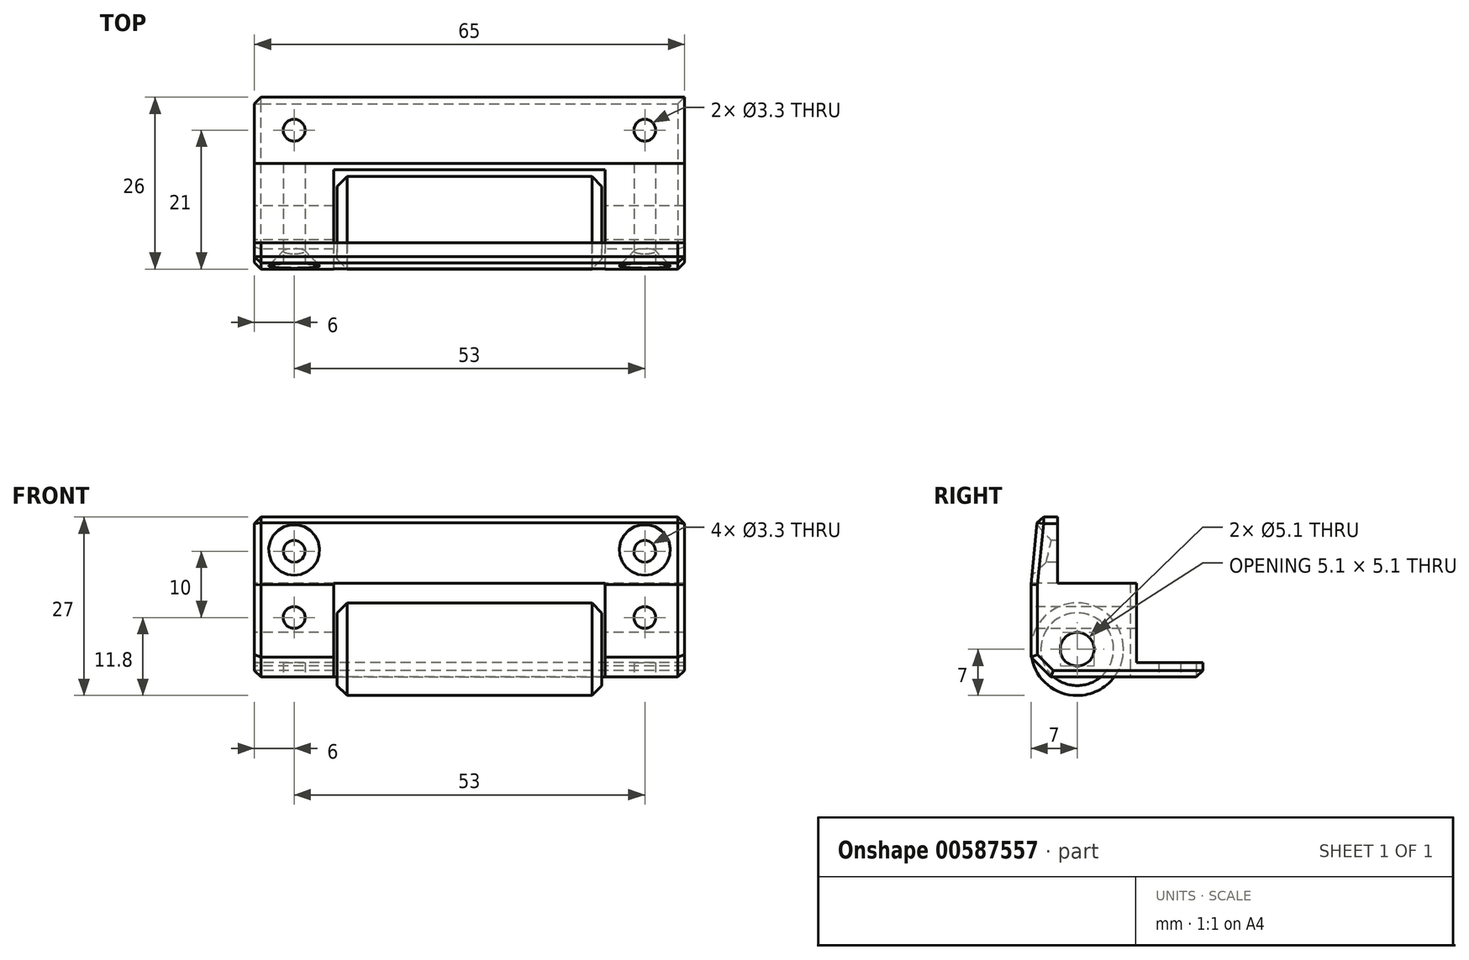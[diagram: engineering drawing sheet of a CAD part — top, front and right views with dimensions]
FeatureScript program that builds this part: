
annotation { "Feature Type Name" : "Feature", "Feature Type Description" : "" }
export const myFeature = defineFeature(function(context is Context, id is Id, definition is map)
    precondition{}
    {
        {
            var Q0;
            Q0=qCreatedBy(makeId("Right.planeOp"),FACE);
            var sketch = newSketch(context, id + "F0", { "sketchPlane" : qUnion([Q0])});
            skLineSegment(sketch, "E0", {"start": v(0, 0) * mm, "end": v(0, 12) * mm});
            skLineSegment(sketch, "E1", {"start": v(0, 12) * mm, "end": v(-12, 12) * mm});
            skLineSegment(sketch, "E2", {"start": v(-12, 12) * mm, "end": v(-12, 22) * mm});
            skLineSegment(sketch, "E3", {"start": v(-12, 22) * mm, "end": v(-15, 22) * mm});
            skLineSegment(sketch, "E4", {"start": v(-16, -2.2) * mm, "end": v(10, -2.2) * mm});
            skLineSegment(sketch, "E5", {"start": v(10, -2.2) * mm, "end": v(10, 0) * mm});
            skLineSegment(sketch, "E6", {"start": v(10, 0) * mm, "end": v(0, 0) * mm});
            skCircle(sketch, "E7", {"center": v(-9, 2) * mm, "radius": 2.55 * mm});
            skCircle(sketch, "E8", {"center": v(-9, 2) * mm, "radius": 7 * mm, "construction": true});
            skLineSegment(sketch, "E9", {"start": v(-16, -2.2) * mm, "end": v(-16, 11.8) * mm});
            skLineSegment(sketch, "E10", {"start": v(-16, 11.8) * mm, "end": v(-15, 22) * mm});
            skSolve(sketch);
        }
        {
            var Q0;
            Q0=makeQuery(id+"F0.imprint","IMPRINT",FACE,{"disambiguationData":[TD([[makeQuery(id+"F0.imprint","IMPRINT",EDGE,{"derivedFrom":sQuery(id+"F0.wireOp",EDGE,"E0")}),1.0]])]});
            extrude(context, id + "F1", {"entities" : qUnion([Q0]), "depth" : 65 * mm, "offsetDistance" : 25 * mm});
        }
        {
            var Q0;
            Q0=makeQuery(id+"F1.opExtrude","SWEPT_FACE",FACE,{"disambiguationData":[OSD([sQuery(id+"F0.wireOp",EDGE,"E9")])]});
            var sketch = newSketch(context, id + "F2", { "sketchPlane" : qUnion([Q0])});
            skLineSegment(sketch, "E11.0.0", {"start": v(0, 22) * mm, "end": v(0, 11.8) * mm, "construction": true});
            skLineSegment(sketch, "E11.0.1", {"start": v(0, 11.8) * mm, "end": v(65, 11.8) * mm, "construction": true});
            skLineSegment(sketch, "E11.0.2", {"start": v(65, 11.8) * mm, "end": v(65, 22) * mm, "construction": true});
            skLineSegment(sketch, "E11.0.3", {"start": v(65, 22) * mm, "end": v(0, 22) * mm, "construction": true});
            skLineSegment(sketch, "E12.0.0", {"start": v(0, 11.8) * mm, "end": v(0, -2.2) * mm, "construction": true});
            skLineSegment(sketch, "E12.0.1", {"start": v(0, -2.2) * mm, "end": v(65, -2.2) * mm, "construction": true});
            skLineSegment(sketch, "E12.0.2", {"start": v(65, -2.2) * mm, "end": v(65, 11.8) * mm, "construction": true});
            skLineSegment(sketch, "E12.0.3", {"start": v(65, 11.8) * mm, "end": v(0, 11.8) * mm, "construction": true});
            skLineSegment(sketch, "E13", {"start": v(32.5, 22) * mm, "end": v(32.5, -2.2) * mm, "construction": true});
            skLineSegment(sketch, "E14.bottom", {"start": v(12, 12) * mm, "end": v(53, 12) * mm});
            skLineSegment(sketch, "E14.top", {"start": v(12, -2.2) * mm, "end": v(53, -2.2) * mm});
            skLineSegment(sketch, "E14.left", {"start": v(12, 12) * mm, "end": v(12, -2.2) * mm});
            skLineSegment(sketch, "E14.right", {"start": v(53, 12) * mm, "end": v(53, -2.2) * mm});
            skLineSegment(sketch, "E15", {"start": v(12, 12) * mm, "end": v(53, -2.2) * mm, "construction": true});
            skLineSegment(sketch, "E16", {"start": v(12, -2.2) * mm, "end": v(53, 12) * mm, "construction": true});
            skPoint(sketch, "E17", {"position": v(32.5, 4.9) * mm});
            skSolve(sketch);
        }
        {
            var Q0;
            Q0=makeQuery(id+"F1.opExtrude","SWEPT_EDGE",EDGE,{"disambiguationData":[OSD([sQuery(id+"F0.wireOp",EDGE,"E4"),sQuery(id+"F0.wireOp",EDGE,"E9")])]});
            chamfer(context, id + "F3", {"entities" : qUnion([Q0]), "width" : 3 * mm, "tangentPropagation" : true});
        }
        {
            var Q0;
            {var subQ0=sQuery(id+"F2.wireOp",EDGE,"E14.top");Q0=makeQuery(id+"F2.imprint","IMPRINT",FACE,{"disambiguationData":[TD([[makeQuery(id+"F2.imprint","IMPRINT",EDGE,{"derivedFrom":subQ0}),-1.0]])]});}
            var Q1;
            {var subQ0=sQuery(id+"F2.wireOp",EDGE,"E14.bottom");Q1=makeQuery(id+"F2.imprint","IMPRINT",FACE,{"disambiguationData":[TD([[makeQuery(id+"F2.imprint","IMPRINT",EDGE,{"derivedFrom":subQ0}),-1.0]])]});}
            extrude(context, id + "F4", {"entities" : qUnion([Q0, Q1]), "operationType" : NewBodyOperationType.REMOVE, "oppositeDirection" : true, "depth" : 15 * mm, "offsetDistance" : 25 * mm});
        }
        {
            var Q0;
            Q0=makeQuery(id+"F4.boolean.opBoolean","COPY",FACE,{"derivedFrom":makeQuery(id+"F4.opExtrude","SWEPT_FACE",FACE,{"disambiguationData":[OSD([sQuery(id+"F2.wireOp",EDGE,"E14.left")])]})});
            cPlane(context, id + "F5", {"entities" : qUnion([Q0]), "cplaneType" : CPlaneType.OFFSET, "offset" : .5 * mm, "width" : 150 * mm, "height" : 150 * mm});
        }
        {
            var Q0;
            Q0=qCreatedBy(id+"F5.planeOp",FACE);
            var sketch = newSketch(context, id + "F6", { "sketchPlane" : qUnion([Q0])});
            skCircle(sketch, "E18.0", {"center": v(-9, 2) * mm, "radius": 2.55 * mm, "construction": true});
            skCircle(sketch, "E19", {"center": v(-9, 2) * mm, "radius": 7 * mm});
            skSolve(sketch);
        }
        {
            var Q0;
            {var subQ1=sQuery(id+"F0.wireOp",EDGE,"E9");Q0=makeQuery(id+"F4.boolean.opBoolean","SPLIT",FACE,{"disambiguationData":[TD([makeQuery(id+"F4.opExtrude","SWEPT_FACE",FACE,{"disambiguationData":[OSD([sQuery(id+"F2.wireOp",EDGE,"E14.left")])]})])],"derivedFrom":makeQuery(id+"F1.opExtrude","SWEPT_FACE",FACE,{"disambiguationData":[OSD([subQ1])]})});}
            var sketch = newSketch(context, id + "F7", { "sketchPlane" : qUnion([Q0])});
            skLineSegment(sketch, "E20.0.0", {"start": v(12, 0.8) * mm, "end": v(12, 11.8) * mm, "construction": true});
            skLineSegment(sketch, "E20.0.1", {"start": v(12, 11.8) * mm, "end": v(0, 11.8) * mm, "construction": true});
            skLineSegment(sketch, "E20.0.2", {"start": v(0, 11.8) * mm, "end": v(0, 0.8) * mm, "construction": true});
            skLineSegment(sketch, "E20.0.3", {"start": v(0, 0.8) * mm, "end": v(12, 0.8) * mm, "construction": true});
            skLineSegment(sketch, "E21.0.0", {"start": v(65, 11.8) * mm, "end": v(53, 11.8) * mm, "construction": true});
            skLineSegment(sketch, "E21.0.1", {"start": v(53, 11.8) * mm, "end": v(53, 0.8) * mm, "construction": true});
            skLineSegment(sketch, "E21.0.2", {"start": v(53, 0.8) * mm, "end": v(65, 0.8) * mm, "construction": true});
            skLineSegment(sketch, "E21.0.3", {"start": v(65, 0.8) * mm, "end": v(65, 11.8) * mm, "construction": true});
            skLineSegment(sketch, "E22", {"start": v(0, 6.8) * mm, "end": v(12, 6.8) * mm, "construction": true});
            skLineSegment(sketch, "E23", {"start": v(53, 6.8) * mm, "end": v(65, 6.8) * mm, "construction": true});
            skCircle(sketch, "E24", {"center": v(59, 6.8) * mm, "radius": 1.65 * mm});
            skCircle(sketch, "E25", {"center": v(6, 6.8) * mm, "radius": 1.65 * mm});
            skLineSegment(sketch, "E26", {"start": v(12, 6.8) * mm, "end": v(53, 6.8) * mm, "construction": true});
            skLineSegment(sketch, "E27", {"start": v(6, 6.8) * mm, "end": v(6, 16.8) * mm, "construction": true});
            skLineSegment(sketch, "E28", {"start": v(59, 6.8) * mm, "end": v(59, 16.8) * mm, "construction": true});
            skPoint(sketch, "E28.endSnap0", {"position": v(59, 11.8) * mm});
            skCircle(sketch, "E29", {"center": v(6, 16.8) * mm, "radius": 1.65 * mm});
            skCircle(sketch, "E30", {"center": v(59, 16.8) * mm, "radius": 1.65 * mm});
            skLineSegment(sketch, "E31", {"start": v(6, 16.8) * mm, "end": v(59, 16.8) * mm, "construction": true});
            skSolve(sketch);
        }
        {
            var Q0;
            Q0=makeQuery(id+"F7.imprint","IMPRINT",FACE,{"disambiguationData":[TD([[makeQuery(id+"F7.imprint","IMPRINT",EDGE,{"derivedFrom":sQuery(id+"F7.wireOp",EDGE,"E25")}),1.0]])]});
            var Q1;
            Q1=makeQuery(id+"F7.imprint","IMPRINT",FACE,{"disambiguationData":[TD([[makeQuery(id+"F7.imprint","IMPRINT",EDGE,{"derivedFrom":sQuery(id+"F7.wireOp",EDGE,"E24")}),1.0]])]});
            var Q2;
            Q2=makeQuery(id+"F7.imprint","IMPRINT",FACE,{"disambiguationData":[TD([[makeQuery(id+"F7.imprint","IMPRINT",EDGE,{"derivedFrom":sQuery(id+"F7.wireOp",EDGE,"E29")}),1.0]])]});
            var Q3;
            Q3=makeQuery(id+"F7.imprint","IMPRINT",FACE,{"disambiguationData":[TD([[makeQuery(id+"F7.imprint","IMPRINT",EDGE,{"derivedFrom":sQuery(id+"F7.wireOp",EDGE,"E30")}),1.0]])]});
            extrude(context, id + "F8", {"entities" : qUnion([Q0, Q1, Q2, Q3]), "operationType" : NewBodyOperationType.REMOVE, "oppositeDirection" : true, "depth" : 25 * mm, "offsetDistance" : 25 * mm});
        }
        {
            var Q0;
            Q0=makeQuery(id+"F6.imprint","IMPRINT",FACE,{"disambiguationData":[TD([[makeQuery(id+"F6.imprint","IMPRINT",EDGE,{"derivedFrom":sQuery(id+"F6.wireOp",EDGE,"E19")}),1.0]])]});
            extrude(context, id + "F9", {"entities" : qUnion([Q0]), "depth" : 40 * mm, "offsetDistance" : 25 * mm});
        }
        {
            var Q0;
            Q0=makeQuery(id+"F9.opExtrude","CAP_EDGE",EDGE,{"disambiguationData":[OSD([sQuery(id+"F6.wireOp",EDGE,"E19")])],"isStart":true});
            var Q1;
            Q1=makeQuery(id+"F9.opExtrude","CAP_EDGE",EDGE,{"disambiguationData":[OSD([sQuery(id+"F6.wireOp",EDGE,"E19")])],"isStart":false});
            chamfer(context, id + "F10", {"entities" : qUnion([Q0, Q1]), "width" : 1.5 * mm, "tangentPropagation" : true});
        }
        {
            var Q0;
            Q0=makeQuery(id+"F1.opExtrude","SWEPT_FACE",FACE,{"disambiguationData":[OSD([sQuery(id+"F0.wireOp",EDGE,"E4")])]});
            var sketch = newSketch(context, id + "F11", { "sketchPlane" : qUnion([Q0])});
            skLineSegment(sketch, "E32.0", {"start": v(65, -10) * mm, "end": v(0, -10) * mm, "construction": true});
            skCircle(sketch, "E33", {"center": v(6, -5) * mm, "radius": 1.65 * mm});
            skCircle(sketch, "E34", {"center": v(59, -5) * mm, "radius": 1.65 * mm});
            skLineSegment(sketch, "E35", {"start": v(6, -5) * mm, "end": v(59, -5) * mm, "construction": true});
            skLineSegment(sketch, "E36", {"start": v(32.5, -5) * mm, "end": v(32.5, -10) * mm, "construction": true});
            skSolve(sketch);
        }
        {
            var Q0;
            Q0=makeQuery(id+"F11.imprint","IMPRINT",FACE,{"disambiguationData":[TD([[makeQuery(id+"F11.imprint","IMPRINT",EDGE,{"derivedFrom":sQuery(id+"F11.wireOp",EDGE,"E33")}),1.0]])]});
            var Q1;
            Q1=makeQuery(id+"F11.imprint","IMPRINT",FACE,{"disambiguationData":[TD([[makeQuery(id+"F11.imprint","IMPRINT",EDGE,{"derivedFrom":sQuery(id+"F11.wireOp",EDGE,"E34")}),1.0]])]});
            extrude(context, id + "F12", {"entities" : qUnion([Q0, Q1]), "operationType" : NewBodyOperationType.REMOVE, "oppositeDirection" : true, "depth" : 25 * mm, "offsetDistance" : 25 * mm});
        }
        {
            var Q0;
            Q0=makeQuery(id+"F8.boolean.opBoolean","COPY",EDGE,{"derivedFrom":makeQuery(id+"F8.opExtrude","CAP_EDGE",EDGE,{"disambiguationData":[OSD([sQuery(id+"F7.wireOp",EDGE,"E25")])],"isStart":true})});
            var Q1;
            Q1=makeQuery(id+"F8.boolean.opBoolean","COPY",EDGE,{"derivedFrom":makeQuery(id+"F8.opExtrude","CAP_EDGE",EDGE,{"disambiguationData":[OSD([sQuery(id+"F7.wireOp",EDGE,"E24")])],"isStart":true})});
            var Q2;
            Q2=makeQuery(id+"F8.boolean.opBoolean","INTERSECT",EDGE,{"derivedFrom":[makeQuery(id+"F1.opExtrude","SWEPT_FACE",FACE,{"disambiguationData":[OSD([sQuery(id+"F0.wireOp",EDGE,"E10")])]}),makeQuery(id+"F8.opExtrude","SWEPT_FACE",FACE,{"disambiguationData":[OSD([sQuery(id+"F7.wireOp",EDGE,"E29")])]})]});
            var Q3;
            Q3=makeQuery(id+"F8.boolean.opBoolean","INTERSECT",EDGE,{"derivedFrom":[makeQuery(id+"F1.opExtrude","SWEPT_FACE",FACE,{"disambiguationData":[OSD([sQuery(id+"F0.wireOp",EDGE,"E10")])]}),makeQuery(id+"F8.opExtrude","SWEPT_FACE",FACE,{"disambiguationData":[OSD([sQuery(id+"F7.wireOp",EDGE,"E30")])]})]});
            var Q4;
            Q4=makeQuery(id+"F12.boolean.opBoolean","COPY",EDGE,{"derivedFrom":makeQuery(id+"F12.opExtrude","CAP_EDGE",EDGE,{"disambiguationData":[OSD([sQuery(id+"F11.wireOp",EDGE,"E33")])],"isStart":true})});
            var Q5;
            Q5=makeQuery(id+"F12.boolean.opBoolean","COPY",EDGE,{"derivedFrom":makeQuery(id+"F12.opExtrude","CAP_EDGE",EDGE,{"disambiguationData":[OSD([sQuery(id+"F11.wireOp",EDGE,"E34")])],"isStart":true})});
            chamfer(context, id + "F13", {"entities" : qUnion([Q0, Q1, Q2, Q3, Q4, Q5]), "width" : 2.2 * mm, "tangentPropagation" : true});
        }
        {
            var Q0;
            Q0=makeQuery(id+"F1.opExtrude","CAP_EDGE",EDGE,{"disambiguationData":[OSD([sQuery(id+"F0.wireOp",EDGE,"E4")])],"isStart":false});
            var Q1;
            Q1=makeQuery(id+"F1.opExtrude","SWEPT_EDGE",EDGE,{"disambiguationData":[OSD([sQuery(id+"F0.wireOp",EDGE,"E4"),sQuery(id+"F0.wireOp",EDGE,"E5")])]});
            var Q2;
            {var subQ0=sQuery(id+"F0.wireOp",EDGE,"E9");var subQ1=sQuery(id+"F0.wireOp",EDGE,"E4");Q2=makeQuery(id+"F3.opChamfer","BLEND_EDGE",EDGE,{"blendedFrom":[makeQuery(id+"F1.opExtrude","SWEPT_EDGE",EDGE,{"disambiguationData":[OSD([subQ1,subQ0])]}),makeQuery(id+"F1.opExtrude","CAP_FACE",FACE,{"disambiguationData":[OSD([sQuery(id+"F0.wireOp",EDGE,"E0"),sQuery(id+"F0.wireOp",EDGE,"E1"),sQuery(id+"F0.wireOp",EDGE,"E2"),sQuery(id+"F0.wireOp",EDGE,"E3"),subQ1,sQuery(id+"F0.wireOp",EDGE,"E5"),sQuery(id+"F0.wireOp",EDGE,"E6"),sQuery(id+"F0.wireOp",EDGE,"E7"),subQ0,sQuery(id+"F0.wireOp",EDGE,"E10")])],"isStart":false})],"blendedInto":[makeQuery(id+"F1.opExtrude","CAP_FACE",FACE,{"disambiguationData":[OSD([sQuery(id+"F0.wireOp",EDGE,"E0"),sQuery(id+"F0.wireOp",EDGE,"E1"),sQuery(id+"F0.wireOp",EDGE,"E2"),sQuery(id+"F0.wireOp",EDGE,"E3"),subQ1,sQuery(id+"F0.wireOp",EDGE,"E5"),sQuery(id+"F0.wireOp",EDGE,"E6"),sQuery(id+"F0.wireOp",EDGE,"E7"),subQ0,sQuery(id+"F0.wireOp",EDGE,"E10")])],"isStart":false})]});}
            var Q3;
            Q3=makeQuery(id+"F1.opExtrude","CAP_EDGE",EDGE,{"disambiguationData":[OSD([sQuery(id+"F0.wireOp",EDGE,"E9")])],"isStart":false});
            var Q4;
            Q4=makeQuery(id+"F1.opExtrude","CAP_EDGE",EDGE,{"disambiguationData":[OSD([sQuery(id+"F0.wireOp",EDGE,"E10")])],"isStart":false});
            var Q5;
            Q5=makeQuery(id+"F1.opExtrude","CAP_EDGE",EDGE,{"disambiguationData":[OSD([sQuery(id+"F0.wireOp",EDGE,"E3")])],"isStart":false});
            var Q6;
            Q6=makeQuery(id+"F1.opExtrude","CAP_EDGE",EDGE,{"disambiguationData":[OSD([sQuery(id+"F0.wireOp",EDGE,"E4")])],"isStart":true});
            var Q7;
            Q7=makeQuery(id+"F1.opExtrude","CAP_EDGE",EDGE,{"disambiguationData":[OSD([sQuery(id+"F0.wireOp",EDGE,"E5")])],"isStart":true});
            var Q8;
            {var subQ0=sQuery(id+"F0.wireOp",EDGE,"E9");var subQ1=sQuery(id+"F0.wireOp",EDGE,"E4");Q8=makeQuery(id+"F3.opChamfer","BLEND_EDGE",EDGE,{"blendedFrom":[makeQuery(id+"F1.opExtrude","SWEPT_EDGE",EDGE,{"disambiguationData":[OSD([subQ1,subQ0])]}),makeQuery(id+"F1.opExtrude","CAP_FACE",FACE,{"disambiguationData":[OSD([sQuery(id+"F0.wireOp",EDGE,"E0"),sQuery(id+"F0.wireOp",EDGE,"E1"),sQuery(id+"F0.wireOp",EDGE,"E2"),sQuery(id+"F0.wireOp",EDGE,"E3"),subQ1,sQuery(id+"F0.wireOp",EDGE,"E5"),sQuery(id+"F0.wireOp",EDGE,"E6"),sQuery(id+"F0.wireOp",EDGE,"E7"),subQ0,sQuery(id+"F0.wireOp",EDGE,"E10")])],"isStart":true})],"blendedInto":[makeQuery(id+"F1.opExtrude","CAP_FACE",FACE,{"disambiguationData":[OSD([sQuery(id+"F0.wireOp",EDGE,"E0"),sQuery(id+"F0.wireOp",EDGE,"E1"),sQuery(id+"F0.wireOp",EDGE,"E2"),sQuery(id+"F0.wireOp",EDGE,"E3"),subQ1,sQuery(id+"F0.wireOp",EDGE,"E5"),sQuery(id+"F0.wireOp",EDGE,"E6"),sQuery(id+"F0.wireOp",EDGE,"E7"),subQ0,sQuery(id+"F0.wireOp",EDGE,"E10")])],"isStart":true})]});}
            var Q9;
            Q9=makeQuery(id+"F1.opExtrude","CAP_EDGE",EDGE,{"disambiguationData":[OSD([sQuery(id+"F0.wireOp",EDGE,"E9")])],"isStart":true});
            var Q10;
            Q10=makeQuery(id+"F1.opExtrude","CAP_EDGE",EDGE,{"disambiguationData":[OSD([sQuery(id+"F0.wireOp",EDGE,"E10")])],"isStart":true});
            var Q11;
            Q11=makeQuery(id+"F1.opExtrude","CAP_EDGE",EDGE,{"disambiguationData":[OSD([sQuery(id+"F0.wireOp",EDGE,"E3")])],"isStart":true});
            var Q12;
            Q12=makeQuery(id+"F1.opExtrude","SWEPT_EDGE",EDGE,{"disambiguationData":[OSD([sQuery(id+"F0.wireOp",EDGE,"E3"),sQuery(id+"F0.wireOp",EDGE,"E10")])]});
            chamfer(context, id + "F14", {"entities" : qUnion([Q0, Q1, Q2, Q3, Q4, Q5, Q6, Q7, Q8, Q9, Q10, Q11, Q12]), "width" : 1 * mm, "tangentPropagation" : true});
        }
    });
